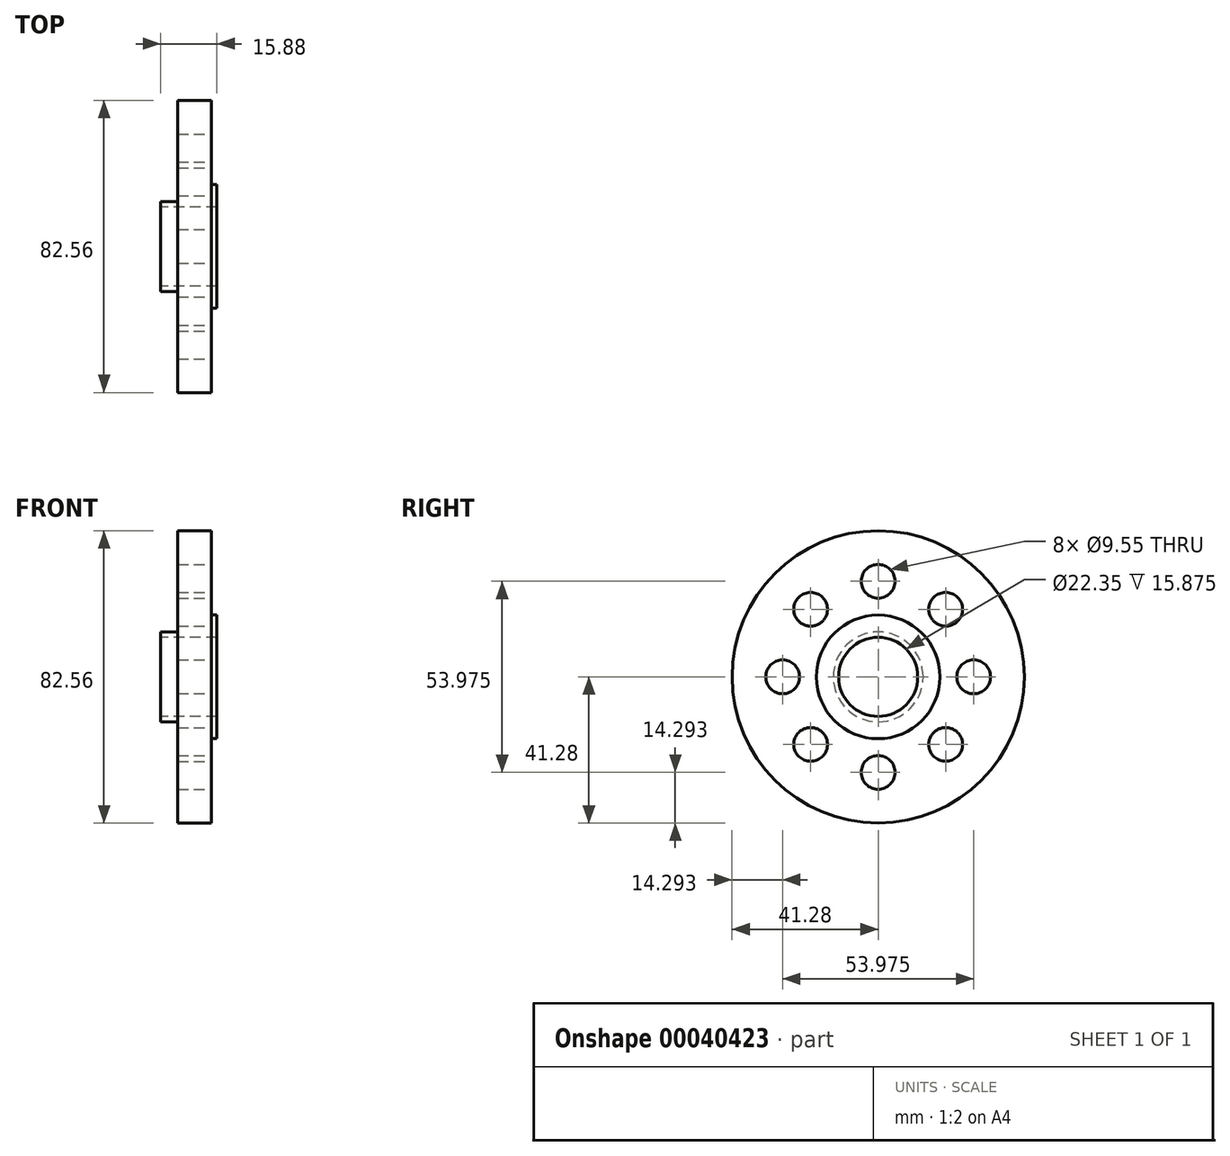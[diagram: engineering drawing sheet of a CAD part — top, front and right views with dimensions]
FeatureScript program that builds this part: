
annotation { "Feature Type Name" : "Feature", "Feature Type Description" : "" }
export const myFeature = defineFeature(function(context is Context, id is Id, definition is map)
    precondition{}
    {
        {
            var Q0;
            Q0=qCreatedBy(makeId("Front.planeOp"),FACE);
            var sketch = newSketch(context, id + "F0", { "sketchPlane" : qUnion([Q0])});
            skLineSegment(sketch, "E0", {"start": v(-7.94, 0) * mm, "end": v(7.94, 0) * mm, "construction": true});
            skPoint(sketch, "E1", {"position": v(0, 0) * mm});
            skLineSegment(sketch, "E2", {"start": v(-7.94, 11.18) * mm, "end": v(7.94, 11.18) * mm});
            skLineSegment(sketch, "E3", {"start": v(7.94, 11.18) * mm, "end": v(7.94, 17.46) * mm});
            skLineSegment(sketch, "E4", {"start": v(7.94, 17.46) * mm, "end": v(6.41, 17.46) * mm});
            skLineSegment(sketch, "E5", {"start": v(6.41, 17.46) * mm, "end": v(6.41, 41.28) * mm});
            skLineSegment(sketch, "E6", {"start": v(6.41, 41.28) * mm, "end": v(-3.16, 41.28) * mm});
            skLineSegment(sketch, "E7", {"start": v(-3.16, 41.28) * mm, "end": v(-3.16, 12.7) * mm});
            skLineSegment(sketch, "E8", {"start": v(-3.16, 12.7) * mm, "end": v(-7.94, 12.7) * mm});
            skLineSegment(sketch, "E9", {"start": v(-7.94, 12.7) * mm, "end": v(-7.94, 11.18) * mm});
            skLineSegment(sketch, "E10", {"start": v(0, 11.18) * mm, "end": v(0, 0) * mm, "construction": true});
            skSolve(sketch);
        }
        {
            var Q0;
            Q0=makeQuery(id+"F0.imprint","IMPRINT",FACE,{"disambiguationData":[TD([[makeQuery(id+"F0.imprint","IMPRINT",EDGE,{"derivedFrom":sQuery(id+"F0.wireOp",EDGE,"E2")}),1.0]])]});
            var Q1;
            Q1=sQuery(id+"F0.wireOp",EDGE,"E0");
            revolve(context, id + "F1", {"entities" : qUnion([Q0]), "axis" : qUnion([Q1]), "revolveType" : RevolveType.FULL});
        }
        {
            var Q0;
            Q0=qCreatedBy(makeId("Right.planeOp"),FACE);
            var sketch = newSketch(context, id + "F2", { "sketchPlane" : qUnion([Q0])});
            skCircle(sketch, "E11", {"center": v(-26.99, 0) * mm, "radius": 4.77 * mm});
            skLineSegment(sketch, "E12", {"start": v(-26.99, 0) * mm, "end": v(0, 0) * mm, "construction": true});
            skCircle(sketch, "E13", {"center": v(0, 0) * mm, "radius": 26.99 * mm, "construction": true});
            skSolve(sketch);
        }
        {
            var Q0;
            Q0 = qSketchRegion(id + "F2", true);
            extrude(context, id + "F3", {"entities" : qUnion([Q0]), "operationType" : NewBodyOperationType.REMOVE, "endBound" : BoundingType.SYMMETRIC, "oppositeDirection" : true, "depth" : 25.4 * mm});
        }
        {
            var Q0;
            Q0=makeQuery(id+"F3.boolean.opBoolean","COPY",FACE,{"derivedFrom":makeQuery(id+"F3.opExtrude","SWEPT_FACE",FACE,{"disambiguationData":[OSD([sQuery(id+"F2.wireOp",EDGE,"E11")])]})});
            var Q1;
            Q1=sQuery(id+"F0.wireOp",EDGE,"E0");
            circularPattern(context, id + "F4", {"faces" : qUnion([Q0]), "axis" : qUnion([Q1]), "angle" : 360 * degree, "instanceCount" : 8, "equalSpace" : true, "patternType" : PatternType.FACE});
        }
    });
